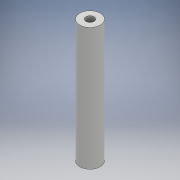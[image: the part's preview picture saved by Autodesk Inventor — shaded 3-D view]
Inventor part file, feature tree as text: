
AUTODESK INVENTOR PART (.ipt)
format: ipt  version: 2017 (Build 210142000, 142)  size: 88,064 bytes
history: native  units: mm
features: extrude x1, sketch x1
ambient origin geometry x8: Origin, YZ Plane, XZ Plane, XY Plane, X Axis, Y Axis, Z Axis, Center Point
bodies: Solid1 (feature_tree)
feature tree (2):
  extrude  "Extrusion1"  Depth=45.0mm
  sketch  "Sketch1"  dims[d0=3.0mm d1=7.5mm d2=45.0mm d3=0.0mm]
